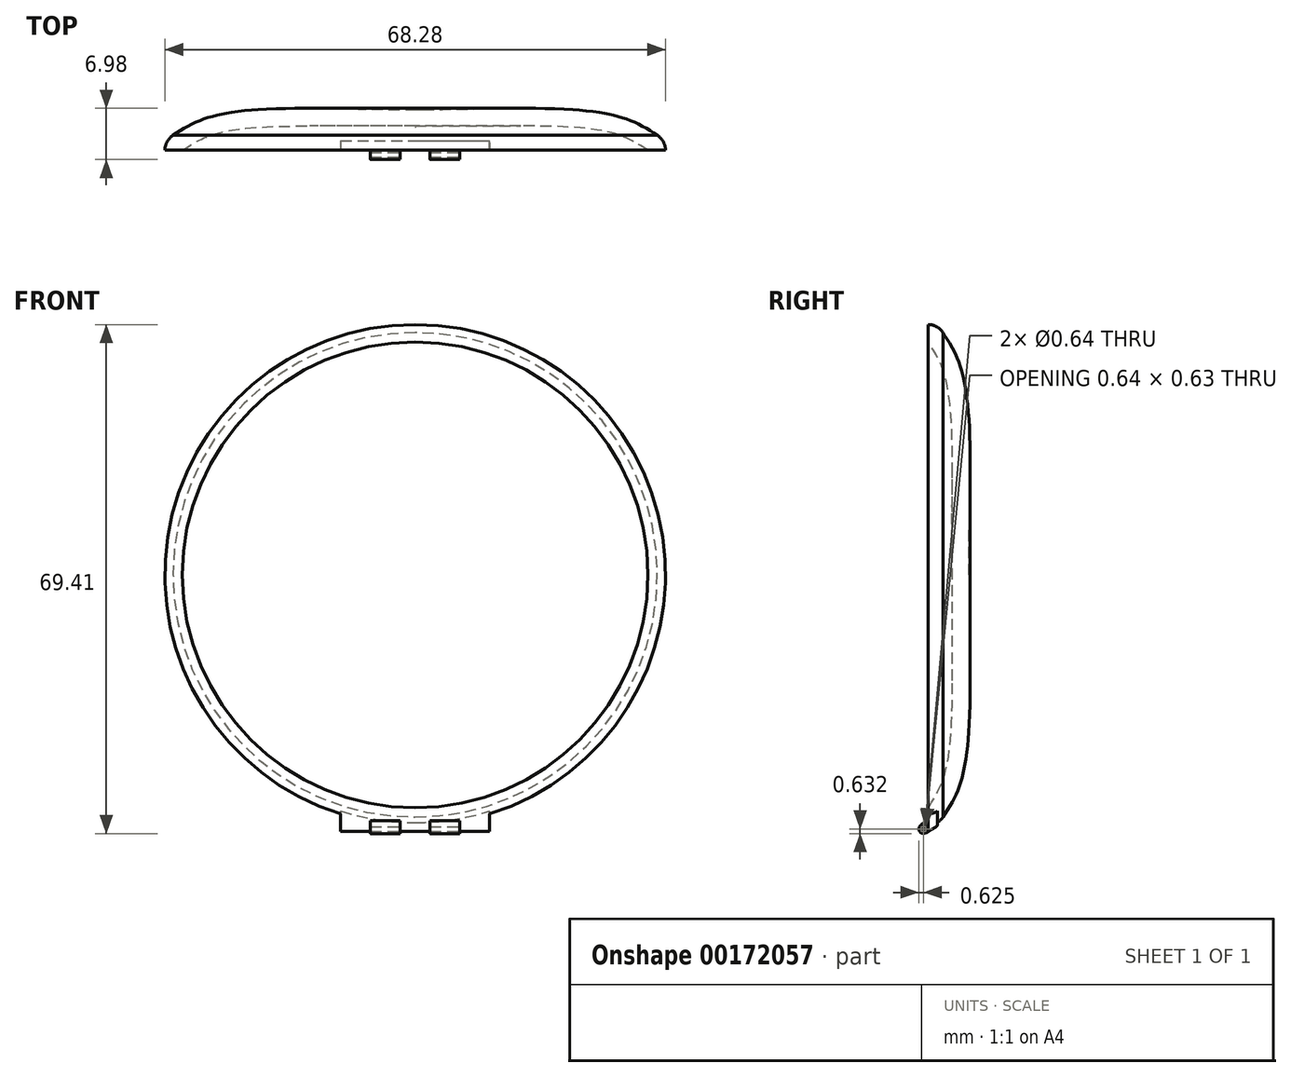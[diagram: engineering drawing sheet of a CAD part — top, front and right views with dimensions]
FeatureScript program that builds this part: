
annotation { "Feature Type Name" : "Feature", "Feature Type Description" : "" }
export const myFeature = defineFeature(function(context is Context, id is Id, definition is map)
    precondition{}
    {
        {
            var Q0;
            Q0=qCreatedBy(makeId("Right.planeOp"),FACE);
            var sketch = newSketch(context, id + "F0", { "sketchPlane" : qUnion([Q0])});
            skPoint(sketch, "E0", {"position": v(3.17, 0) * mm});
            skFitSpline(sketch, "E1", {"points": [v(3.18, 0) * mm, v(2.45, 26.5) * mm, v(0, 31.75) * mm], "startDerivative": vector(0, 46.42) * mm, "endDerivative": vector(-7.5, 11.95) * mm});
            skFitSpline(sketch, "E2.0", {"points": [v(5.56, 0) * mm, v(5.56, 1.92) * mm, v(5.6, 5.76) * mm, v(5.69, 11.37) * mm, v(5.7, 16.65) * mm, v(5.6, 20.62) * mm, v(5.37, 23.48) * mm, v(5.15, 25.13) * mm, v(4.93, 26.35) * mm, v(4.73, 27.23) * mm, v(4.5, 28.06) * mm, v(4.16, 29.07) * mm, v(3.68, 30.2) * mm, v(2.88, 31.72) * mm, v(2.31, 32.56) * mm, v(2.02, 33.02) * mm]});
            skLineSegment(sketch, "E3", {"start": v(0, 34.14) * mm, "end": v(0, 31.75) * mm});
            skArc(sketch, "E4", {"start": v(2.02, 33.02) * mm, "mid": v(1.16, 33.84) * mm, "end": v(0, 34.14) * mm});
            skLineSegment(sketch, "E5", {"start": v(3.18, 0) * mm, "end": v(5.56, 0) * mm});
            skLineSegment(sketch, "E6", {"start": v(0, 0) * mm, "end": v(5.56, 0) * mm, "construction": true});
            skSolve(sketch);
        }
        {
            var Q0;
            Q0=makeQuery(id+"F0.imprint","IMPRINT",FACE,{"disambiguationData":[TD([[makeQuery(id+"F0.imprint","IMPRINT",EDGE,{"derivedFrom":sQuery(id+"F0.wireOp",EDGE,"E1")}),-1.0]])]});
            var Q1;
            Q1=sQuery(id+"F0.wireOp",EDGE,"E6");
            revolve(context, id + "F1", {"entities" : qUnion([Q0]), "axis" : qUnion([Q1]), "revolveType" : RevolveType.FULL});
        }
        {
            var Q0;
            Q0=makeQuery(id+"F1.opRevolve","SWEPT_FACE",FACE,{"disambiguationData":[OSD([sQuery(id+"F0.wireOp",EDGE,"E3")])]});
            var sketch = newSketch(context, id + "F2", { "sketchPlane" : qUnion([Q0])});
            skArc(sketch, "E7", {"start": v(-10.16, -30.08) * mm, "mid": v(0, -31.75) * mm, "end": v(10.16, -30.08) * mm});
            skLineSegment(sketch, "E8", {"start": v(0, 0) * mm, "end": v(0, -51.92) * mm, "construction": true});
            skLineSegment(sketch, "E9", {"start": v(-10.16, -30.08) * mm, "end": v(-10.16, -34.27) * mm});
            skLineSegment(sketch, "E10", {"start": v(-10.16, -34.27) * mm, "end": v(10.16, -34.27) * mm});
            skLineSegment(sketch, "E11", {"start": v(10.16, -34.27) * mm, "end": v(10.16, -30.08) * mm});
            skSolve(sketch);
        }
        {
            var Q0;
            Q0 = qSketchRegion(id + "F2", true);
            extrude(context, id + "F3", {"entities" : qUnion([Q0]), "operationType" : NewBodyOperationType.ADD, "oppositeDirection" : true, "depth" : 1.27 * mm});
        }
        {
            var Q0;
            Q0=makeQuery(id+"F3.opExtrude","SWEPT_FACE",FACE,{"disambiguationData":[OSD([sQuery(id+"F2.wireOp",EDGE,"E11")])]});
            var sketch = newSketch(context, id + "F4", { "sketchPlane" : qUnion([Q0])});
            skLineSegment(sketch, "E12", {"start": v(1.27, -34.27) * mm, "end": v(-0.86, -35.5) * mm});
            skLineSegment(sketch, "E13", {"start": v(-0.86, -35.5) * mm, "end": v(-1.5, -34.4) * mm});
            skLineSegment(sketch, "E14", {"start": v(-1.5, -34.4) * mm, "end": v(0.64, -33.17) * mm});
            skLineSegment(sketch, "E15", {"start": v(0.64, -33.17) * mm, "end": v(1.27, -34.27) * mm});
            skSolve(sketch);
        }
        {
            var Q0;
            Q0 = qSketchRegion(id + "F4", true);
            extrude(context, id + "F5", {"entities" : qUnion([Q0]), "operationType" : NewBodyOperationType.ADD, "oppositeDirection" : true, "depth" : 20.32 * mm});
        }
        {
            var Q0;
            Q0=makeQuery(id+"F4.imprint","IMPRINT",FACE,{"disambiguationData":[TD([[makeQuery(id+"F4.imprint","IMPRINT",EDGE,{"derivedFrom":sQuery(id+"F4.wireOp",EDGE,"E12")}),-1.0]])]});
            var sketch = newSketch(context, id + "F6", { "sketchPlane" : qUnion([Q0])});
            skCircle(sketch, "E16", {"center": v(-0.64, -34.64) * mm, "radius": 0.32 * mm});
            skLineSegment(sketch, "E17", {"start": v(-1.45, -33.22) * mm, "end": v(0.36, -36.36) * mm, "construction": true});
            skLineSegment(sketch, "E18", {"start": v(-0.32, -35.19) * mm, "end": v(-0.86, -35.5) * mm});
            skLineSegment(sketch, "E19", {"start": v(-0.86, -35.5) * mm, "end": v(-1.18, -34.95) * mm});
            skArc(sketch, "E20", {"start": v(-1.18, -34.95) * mm, "mid": v(-0.8, -35.25) * mm, "end": v(-0.32, -35.19) * mm});
            skSolve(sketch);
        }
        {
            var Q0;
            Q0 = qSketchRegion(id + "F6", true);
            extrude(context, id + "F7", {"entities" : qUnion([Q0]), "operationType" : NewBodyOperationType.REMOVE, "endBound" : BoundingType.THROUGH_ALL, "oppositeDirection" : true, "depth" : 25.4 * mm});
        }
        {
            var Q0;
            Q0=makeQuery(id+"F5.opExtrude","SWEPT_EDGE",EDGE,{"disambiguationData":[OSD([sQuery(id+"F4.wireOp",EDGE,"E13"),sQuery(id+"F4.wireOp",EDGE,"E14")])]});
            fillet(context, id + "F8", {"entities" : qUnion([Q0]), "radius" : 0.64 * mm, "tangentPropagation" : true, "allowEdgeOverflow" : false});
        }
        {
            var Q0;
            Q0=qCreatedBy(makeId("Front.planeOp"),FACE);
            cPlane(context, id + "F9", {"entities" : qUnion([Q0]), "cplaneType" : CPlaneType.OFFSET, "offset" : 1.27 * mm, "width" : 152.4 * mm, "height" : 152.4 * mm});
        }
        {
            var Q0;
            Q0=qCreatedBy(id+"F9.planeOp",FACE);
            var sketch = newSketch(context, id + "F10", { "sketchPlane" : qUnion([Q0])});
            skLineSegment(sketch, "E21", {"start": v(-6.1, -36.05) * mm, "end": v(-6.1, -31.85) * mm});
            skLineSegment(sketch, "E22", {"start": v(-2.03, -31.85) * mm, "end": v(-2.03, -36.1) * mm});
            skLineSegment(sketch, "E23", {"start": v(2.04, -36.1) * mm, "end": v(2.04, -31.85) * mm});
            skLineSegment(sketch, "E24", {"start": v(6.1, -31.85) * mm, "end": v(6.1, -36.65) * mm});
            skLineSegment(sketch, "E25", {"start": v(-6.1, -36.05) * mm, "end": v(-10.16, -36.05) * mm});
            skLineSegment(sketch, "E26", {"start": v(-10.16, -36.05) * mm, "end": v(-10.16, -31.85) * mm});
            skLineSegment(sketch, "E27", {"start": v(-10.16, -31.85) * mm, "end": v(-6.1, -31.85) * mm});
            skLineSegment(sketch, "E28", {"start": v(-2.03, -31.85) * mm, "end": v(2.04, -31.85) * mm});
            skLineSegment(sketch, "E29", {"start": v(-2.03, -36.1) * mm, "end": v(2.04, -36.1) * mm});
            skLineSegment(sketch, "E30", {"start": v(6.1, -31.85) * mm, "end": v(10.16, -31.85) * mm});
            skLineSegment(sketch, "E31", {"start": v(10.16, -31.85) * mm, "end": v(10.16, -36.65) * mm});
            skLineSegment(sketch, "E32", {"start": v(10.16, -36.65) * mm, "end": v(6.1, -36.65) * mm});
            skLineSegment(sketch, "E33", {"start": v(-17.75, -31.85) * mm, "end": v(17.12, -31.85) * mm, "construction": true});
            skSolve(sketch);
        }
        {
            var Q0;
            Q0 = qSketchRegion(id + "F10", true);
            extrude(context, id + "F11", {"entities" : qUnion([Q0]), "operationType" : NewBodyOperationType.REMOVE, "oppositeDirection" : true, "depth" : 1.27 * mm});
        }
        {
            var Q0;
            {var subQ0=sQuery(id+"F2.wireOp",EDGE,"E10");Q0=makeQuery(id+"F5.boolean.opBoolean","MERGE",EDGE,{"derivedFrom":[makeQuery(id+"F3.opExtrude","CAP_EDGE",EDGE,{"disambiguationData":[OSD([subQ0])],"isStart":false}),makeQuery(id+"F5.opExtrude","SWEPT_EDGE",EDGE,{"disambiguationData":[OSD([subQ0,sQuery(id+"F2.wireOp",EDGE,"E11"),sQuery(id+"F4.wireOp",EDGE,"E12"),sQuery(id+"F4.wireOp",EDGE,"E15")])]})]});}
            fillet(context, id + "F12", {"entities" : qUnion([Q0]), "radius" : 0.5 * mm, "tangentPropagation" : true, "allowEdgeOverflow" : false});
        }
    });
